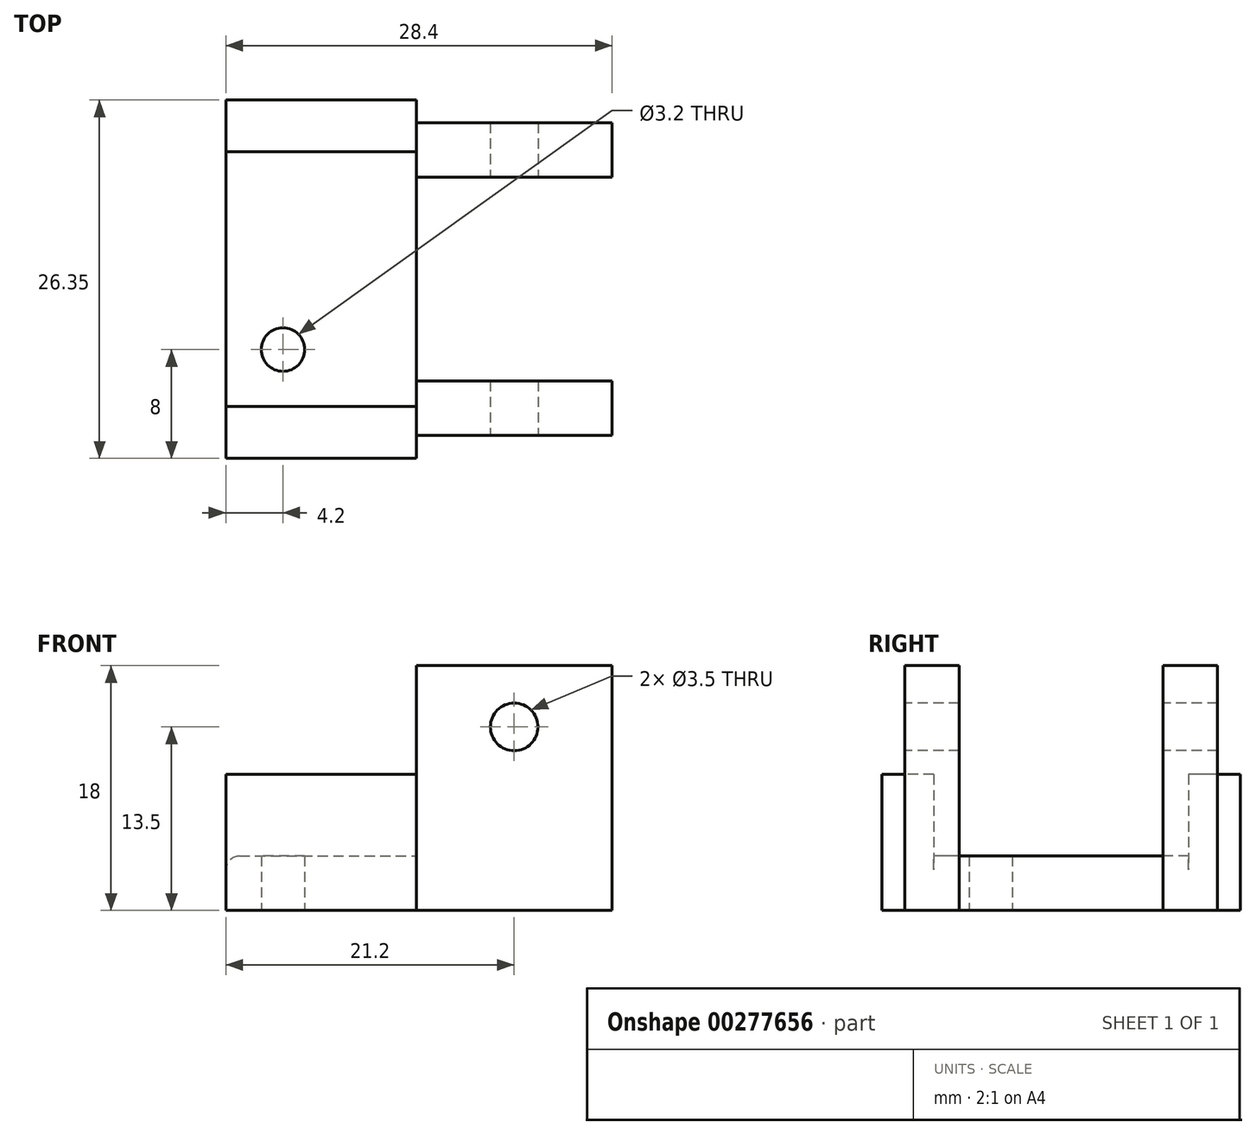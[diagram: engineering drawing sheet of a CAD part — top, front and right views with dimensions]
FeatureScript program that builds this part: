
annotation { "Feature Type Name" : "Feature", "Feature Type Description" : "" }
export const myFeature = defineFeature(function(context is Context, id is Id, definition is map)
    precondition{}
    {
        {
            var Q0;
            Q0=qCreatedBy(makeId("Top.planeOp"),FACE);
            var sketch = newSketch(context, id + "F0", { "sketchPlane" : qUnion([Q0])});
            skLineSegment(sketch, "E0.bottom", {"start": v(0, 0) * mm, "end": v(14, 0) * mm});
            skLineSegment(sketch, "E0.top", {"start": v(0, -18.75) * mm, "end": v(14, -18.75) * mm});
            skLineSegment(sketch, "E0.left", {"start": v(0, 0) * mm, "end": v(0, -18.75) * mm});
            skLineSegment(sketch, "E0.right", {"start": v(14, 0) * mm, "end": v(14, -18.75) * mm});
            skCircle(sketch, "E1", {"center": v(4.2, -14.55) * mm, "radius": 1.6 * mm});
            skLineSegment(sketch, "E2.bottom", {"start": v(0, 3.8) * mm, "end": v(14, 3.8) * mm});
            skLineSegment(sketch, "E2.left", {"start": v(0, 3.8) * mm, "end": v(0, 0) * mm});
            skLineSegment(sketch, "E2.right", {"start": v(14, 3.8) * mm, "end": v(14, 0) * mm});
            skLineSegment(sketch, "E3.top", {"start": v(0, -22.55) * mm, "end": v(14, -22.55) * mm});
            skLineSegment(sketch, "E3.left", {"start": v(0, -18.75) * mm, "end": v(0, -22.55) * mm});
            skLineSegment(sketch, "E3.right", {"start": v(14, -18.75) * mm, "end": v(14, -22.55) * mm});
            skLineSegment(sketch, "E4", {"start": v(4.2, -14.55) * mm, "end": v(21.2, -14.55) * mm, "construction": true});
            skLineSegment(sketch, "E5.bottom", {"start": v(14, -16.87) * mm, "end": v(28.4, -16.87) * mm});
            skLineSegment(sketch, "E5.top", {"start": v(14, -20.87) * mm, "end": v(28.4, -20.87) * mm});
            skLineSegment(sketch, "E5.left", {"start": v(14, -16.87) * mm, "end": v(14, -20.87) * mm});
            skLineSegment(sketch, "E5.right", {"start": v(28.4, -16.87) * mm, "end": v(28.4, -20.87) * mm});
            skLineSegment(sketch, "E6.bottom", {"start": v(14, -1.87) * mm, "end": v(28.4, -1.87) * mm});
            skLineSegment(sketch, "E6.top", {"start": v(14, 2.13) * mm, "end": v(28.4, 2.13) * mm});
            skLineSegment(sketch, "E6.left", {"start": v(14, -1.87) * mm, "end": v(14, 2.13) * mm});
            skLineSegment(sketch, "E6.right", {"start": v(28.4, -1.87) * mm, "end": v(28.4, 2.13) * mm});
            skPoint(sketch, "E7", {"position": v(14, -9.37) * mm});
            skLineSegment(sketch, "E8", {"start": v(28.4, -1.87) * mm, "end": v(28.4, -16.87) * mm, "construction": true});
            skPoint(sketch, "E9", {"position": v(28.4, -9.37) * mm});
            skLineSegment(sketch, "E10", {"start": v(14, -9.37) * mm, "end": v(28.4, -9.37) * mm, "construction": true});
            skPoint(sketch, "E11", {"position": v(21.2, -16.87) * mm});
            skPoint(sketch, "E12", {"position": v(21.2, -1.87) * mm});
            skLineSegment(sketch, "E13", {"start": v(21.2, -1.87) * mm, "end": v(21.2, -16.87) * mm, "construction": true});
            skSolve(sketch);
        }
        {
            var Q0;
            Q0=makeQuery(id+"F0.imprint","IMPRINT",FACE,{"disambiguationData":[TD([[makeQuery(id+"F0.imprint","IMPRINT",EDGE,{"derivedFrom":sQuery(id+"F0.wireOp",EDGE,"E0.left")}),1.0]])]});
            extrude(context, id + "F1", {"entities" : qUnion([Q0]), "depth" : 4 * mm});
        }
        {
            var Q0;
            Q0=makeQuery(id+"F0.imprint","IMPRINT",FACE,{"disambiguationData":[TD([[makeQuery(id+"F0.imprint","IMPRINT",EDGE,{"derivedFrom":sQuery(id+"F0.wireOp",EDGE,"E2.bottom")}),-1.0]])]});
            var Q1;
            {var subQ1=sQuery(id+"F0.wireOp",EDGE,"E0.top");Q1=makeQuery(id+"F0.imprint","IMPRINT",FACE,{"disambiguationData":[TD([[makeQuery(id+"F0.imprint","IMPRINT",EDGE,{"derivedFrom":subQ1}),-1.0]])]});}
            extrude(context, id + "F2", {"entities" : qUnion([Q0, Q1]), "operationType" : NewBodyOperationType.ADD, "depth" : 10 * mm});
        }
        {
            var Q0;
            {var subQ3=sQuery(id+"F0.wireOp",EDGE,"E6.bottom");Q0=makeQuery(id+"F0.imprint","IMPRINT",FACE,{"disambiguationData":[TD([[makeQuery(id+"F0.imprint","IMPRINT",EDGE,{"derivedFrom":subQ3}),1.0]])]});}
            var Q1;
            {var subQ3=sQuery(id+"F0.wireOp",EDGE,"E5.bottom");Q1=makeQuery(id+"F0.imprint","IMPRINT",FACE,{"disambiguationData":[TD([[makeQuery(id+"F0.imprint","IMPRINT",EDGE,{"derivedFrom":subQ3}),-1.0]])]});}
            extrude(context, id + "F3", {"entities" : qUnion([Q0, Q1]), "operationType" : NewBodyOperationType.ADD, "depth" : 18 * mm});
        }
        {
            var Q0;
            Q0=makeQuery(id+"F3.opExtrude","SWEPT_FACE",FACE,{"disambiguationData":[OSD([sQuery(id+"F0.wireOp",EDGE,"E5.top")])]});
            var sketch = newSketch(context, id + "F4", { "sketchPlane" : qUnion([Q0])});
            skCircle(sketch, "E14", {"center": v(21.2, 13.5) * mm, "radius": 1.75 * mm});
            skPoint(sketch, "E15", {"position": v(21.2, 0) * mm});
            skPoint(sketch, "E16", {"position": v(21.2, 18) * mm});
            skSolve(sketch);
        }
        {
            var Q0;
            Q0=makeQuery(id+"F4.imprint","IMPRINT",FACE,{"disambiguationData":[TD([[makeQuery(id+"F4.imprint","IMPRINT",EDGE,{"derivedFrom":sQuery(id+"F4.wireOp",EDGE,"E14")}),1.0]])]});
            var Q1;
            Q1=makeQuery(id+"F3.opExtrude","SWEPT_FACE",FACE,{"disambiguationData":[OSD([sQuery(id+"F0.wireOp",EDGE,"E6.top")])]});
            extrude(context, id + "F5", {"entities" : qUnion([Q0]), "operationType" : NewBodyOperationType.REMOVE, "endBound" : BoundingType.UP_TO_SURFACE, "oppositeDirection" : true, "endBoundEntityFace" : qUnion([Q1]), "depth" : 25 * mm});
        }
        {
            var Q0;
            Q0=makeQuery(id+"F1.opExtrude","CAP_EDGE",EDGE,{"disambiguationData":[OSD([sQuery(id+"F0.wireOp",EDGE,"E0.left")])],"isStart":false});
            fillet(context, id + "F6", {"entities" : qUnion([Q0]), "radius" : 1 * mm, "tangentPropagation" : true, "allowEdgeOverflow" : false});
        }
    });
